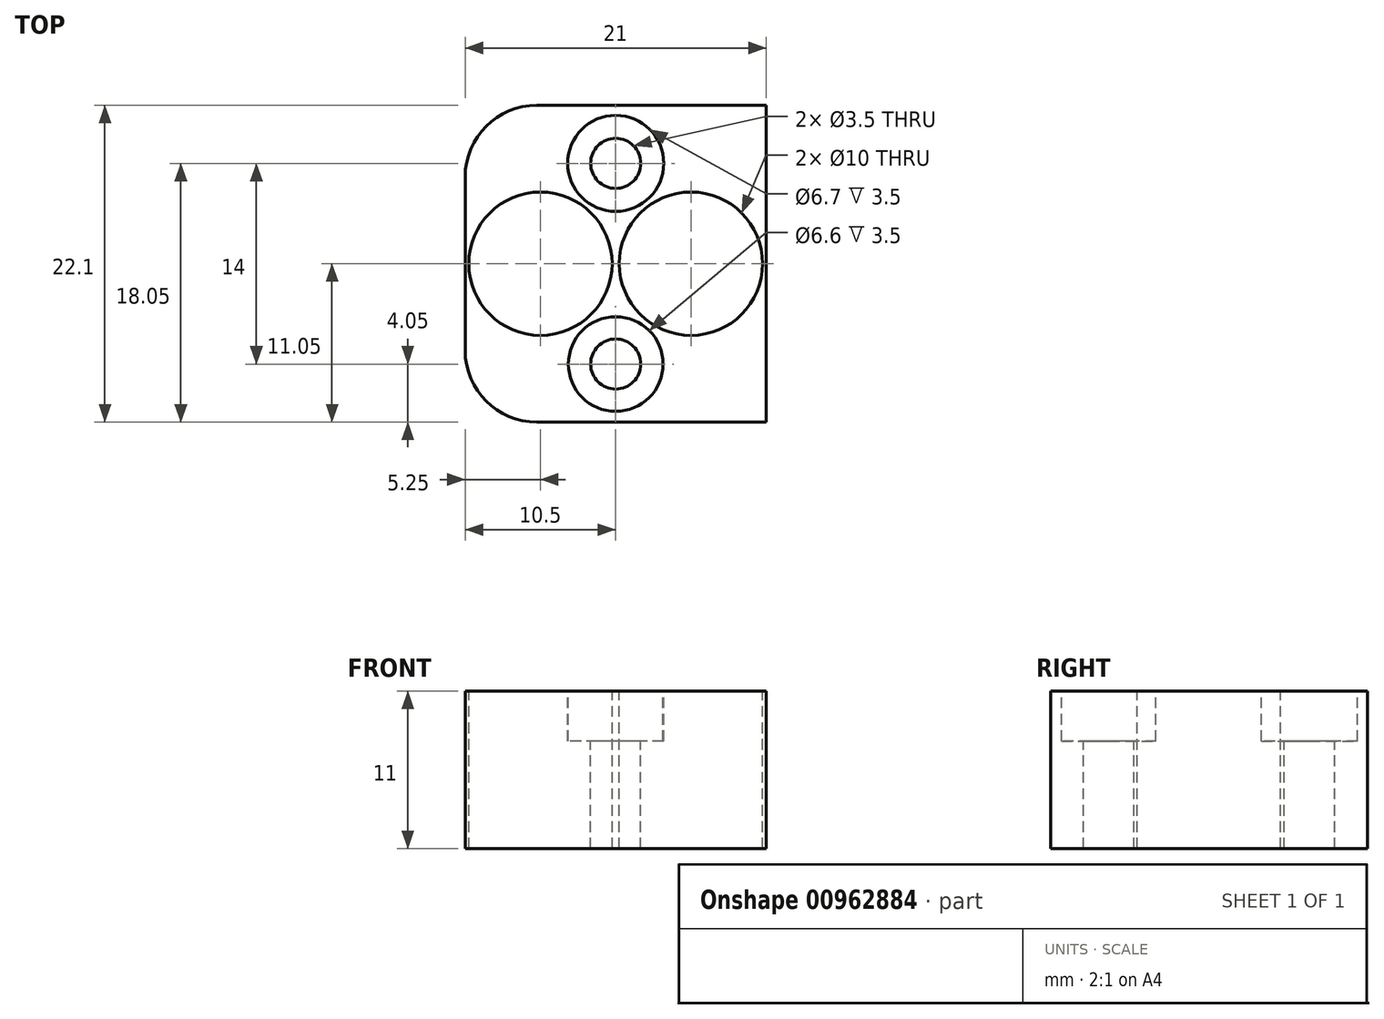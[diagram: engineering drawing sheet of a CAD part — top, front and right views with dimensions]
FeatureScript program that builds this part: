
annotation { "Feature Type Name" : "Feature", "Feature Type Description" : "" }
export const myFeature = defineFeature(function(context is Context, id is Id, definition is map)
    precondition{}
    {
        {
            var Q0;
            Q0=qCreatedBy(makeId("Top.planeOp"),FACE);
            var sketch = newSketch(context, id + "F0", { "sketchPlane" : qUnion([Q0])});
            skLineSegment(sketch, "E0.bottom", {"start": v(0, 0) * mm, "end": v(21, 0) * mm});
            skLineSegment(sketch, "E0.top", {"start": v(0, 22.1) * mm, "end": v(21, 22.1) * mm});
            skLineSegment(sketch, "E0.left", {"start": v(0, 0) * mm, "end": v(0, 22.1) * mm});
            skLineSegment(sketch, "E0.right", {"start": v(21, 0) * mm, "end": v(21, 22.1) * mm});
            skSolve(sketch);
        }
        {
            var Q0;
            Q0 = qSketchRegion(id + "F0", true);
            extrude(context, id + "F1", {"entities" : qUnion([Q0]), "depth" : 11 * mm, "offsetDistance" : 25 * mm});
        }
        {
            var Q0;
            Q0=makeQuery(id+"F1.opExtrude","CAP_FACE",FACE,{"disambiguationData":[OSD([sQuery(id+"F0.wireOp",EDGE,"E0.bottom"),sQuery(id+"F0.wireOp",EDGE,"E0.top"),sQuery(id+"F0.wireOp",EDGE,"E0.left"),sQuery(id+"F0.wireOp",EDGE,"E0.right")])],"isStart":false});
            var sketch = newSketch(context, id + "F2", { "sketchPlane" : qUnion([Q0])});
            skLineSegment(sketch, "E1", {"start": v(10.5, 22.1) * mm, "end": v(10.5, 0) * mm, "construction": true});
            skCircle(sketch, "E2", {"center": v(10.5, 18.05) * mm, "radius": 1.75 * mm});
            skCircle(sketch, "E3", {"center": v(10.5, 4.05) * mm, "radius": 1.75 * mm});
            skLineSegment(sketch, "E4", {"start": v(0, 11.05) * mm, "end": v(21, 11.05) * mm, "construction": true});
            skCircle(sketch, "E5", {"center": v(10.5, 18.05) * mm, "radius": 3.35 * mm});
            skCircle(sketch, "E6", {"center": v(10.5, 4.05) * mm, "radius": 3.3 * mm});
            skSolve(sketch);
        }
        {
            var Q0;
            Q0=makeQuery(id+"F2.imprint","IMPRINT",FACE,{"disambiguationData":[TD([[makeQuery(id+"F2.imprint","IMPRINT",EDGE,{"derivedFrom":sQuery(id+"F2.wireOp",EDGE,"E2")}),1.0]])]});
            var Q1;
            Q1=makeQuery(id+"F2.imprint","IMPRINT",FACE,{"disambiguationData":[TD([[makeQuery(id+"F2.imprint","IMPRINT",EDGE,{"derivedFrom":sQuery(id+"F2.wireOp",EDGE,"E3")}),1.0]])]});
            extrude(context, id + "F3", {"entities" : qUnion([Q0, Q1]), "operationType" : NewBodyOperationType.REMOVE, "oppositeDirection" : true, "depth" : 25 * mm, "offsetDistance" : 25 * mm});
        }
        {
            var Q0;
            Q0=makeQuery(id+"F2.imprint","IMPRINT",FACE,{"disambiguationData":[TD([[makeQuery(id+"F2.imprint","IMPRINT",EDGE,{"derivedFrom":sQuery(id+"F2.wireOp",EDGE,"E2")}),-1.0]])]});
            var Q1;
            Q1=makeQuery(id+"F2.imprint","IMPRINT",FACE,{"disambiguationData":[TD([[makeQuery(id+"F2.imprint","IMPRINT",EDGE,{"derivedFrom":sQuery(id+"F2.wireOp",EDGE,"E3")}),-1.0]])]});
            extrude(context, id + "F4", {"entities" : qUnion([Q0, Q1]), "operationType" : NewBodyOperationType.REMOVE, "oppositeDirection" : true, "depth" : 3.5 * mm, "offsetDistance" : 25 * mm});
        }
        {
            var Q0;
            Q0=makeQuery(id+"F2.imprint","IMPRINT",FACE,{"disambiguationData":[TD([[makeQuery(id+"F2.imprint","IMPRINT",EDGE,{"derivedFrom":sQuery(id+"F2.wireOp",EDGE,"E5")}),-1.0]])]});
            var sketch = newSketch(context, id + "F5", { "sketchPlane" : qUnion([Q0])});
            skLineSegment(sketch, "E7.0", {"start": v(0, 11.05) * mm, "end": v(21, 11.05) * mm, "construction": true});
            skLineSegment(sketch, "E8.0", {"start": v(10.5, 22.1) * mm, "end": v(10.5, 0) * mm, "construction": true});
            skCircle(sketch, "E9", {"center": v(5.25, 11.05) * mm, "radius": 5 * mm});
            skCircle(sketch, "E10", {"center": v(15.75, 11.05) * mm, "radius": 5 * mm});
            skLineSegment(sketch, "E11.0", {"start": v(0, 0) * mm, "end": v(0, 22.1) * mm});
            skLineSegment(sketch, "E12.0", {"start": v(21, 0) * mm, "end": v(21, 22.1) * mm});
            skSolve(sketch);
        }
        {
            var Q0;
            Q0=makeQuery(id+"F1.opExtrude","SWEPT_EDGE",EDGE,{"disambiguationData":[OSD([sQuery(id+"F0.wireOp",EDGE,"E0.top"),sQuery(id+"F0.wireOp",EDGE,"E0.left")])]});
            var Q1;
            Q1=makeQuery(id+"F1.opExtrude","SWEPT_EDGE",EDGE,{"disambiguationData":[OSD([sQuery(id+"F0.wireOp",EDGE,"E0.bottom"),sQuery(id+"F0.wireOp",EDGE,"E0.left")])]});
            fillet(context, id + "F6", {"entities" : qUnion([Q0, Q1]), "radius" : 5 * mm, "tangentPropagation" : true, "allowEdgeOverflow" : false});
        }
        {
            var Q0;
            Q0=makeQuery(id+"F5.imprint","IMPRINT",FACE,{"disambiguationData":[TD([[makeQuery(id+"F5.imprint","IMPRINT",EDGE,{"derivedFrom":sQuery(id+"F5.wireOp",EDGE,"E9")}),1.0]])]});
            var Q1;
            Q1=makeQuery(id+"F5.imprint","IMPRINT",FACE,{"disambiguationData":[TD([[makeQuery(id+"F5.imprint","IMPRINT",EDGE,{"derivedFrom":sQuery(id+"F5.wireOp",EDGE,"E10")}),1.0]])]});
            extrude(context, id + "F7", {"entities" : qUnion([Q0, Q1]), "operationType" : NewBodyOperationType.REMOVE, "oppositeDirection" : true, "depth" : 25 * mm, "offsetDistance" : 25 * mm});
        }
    });
